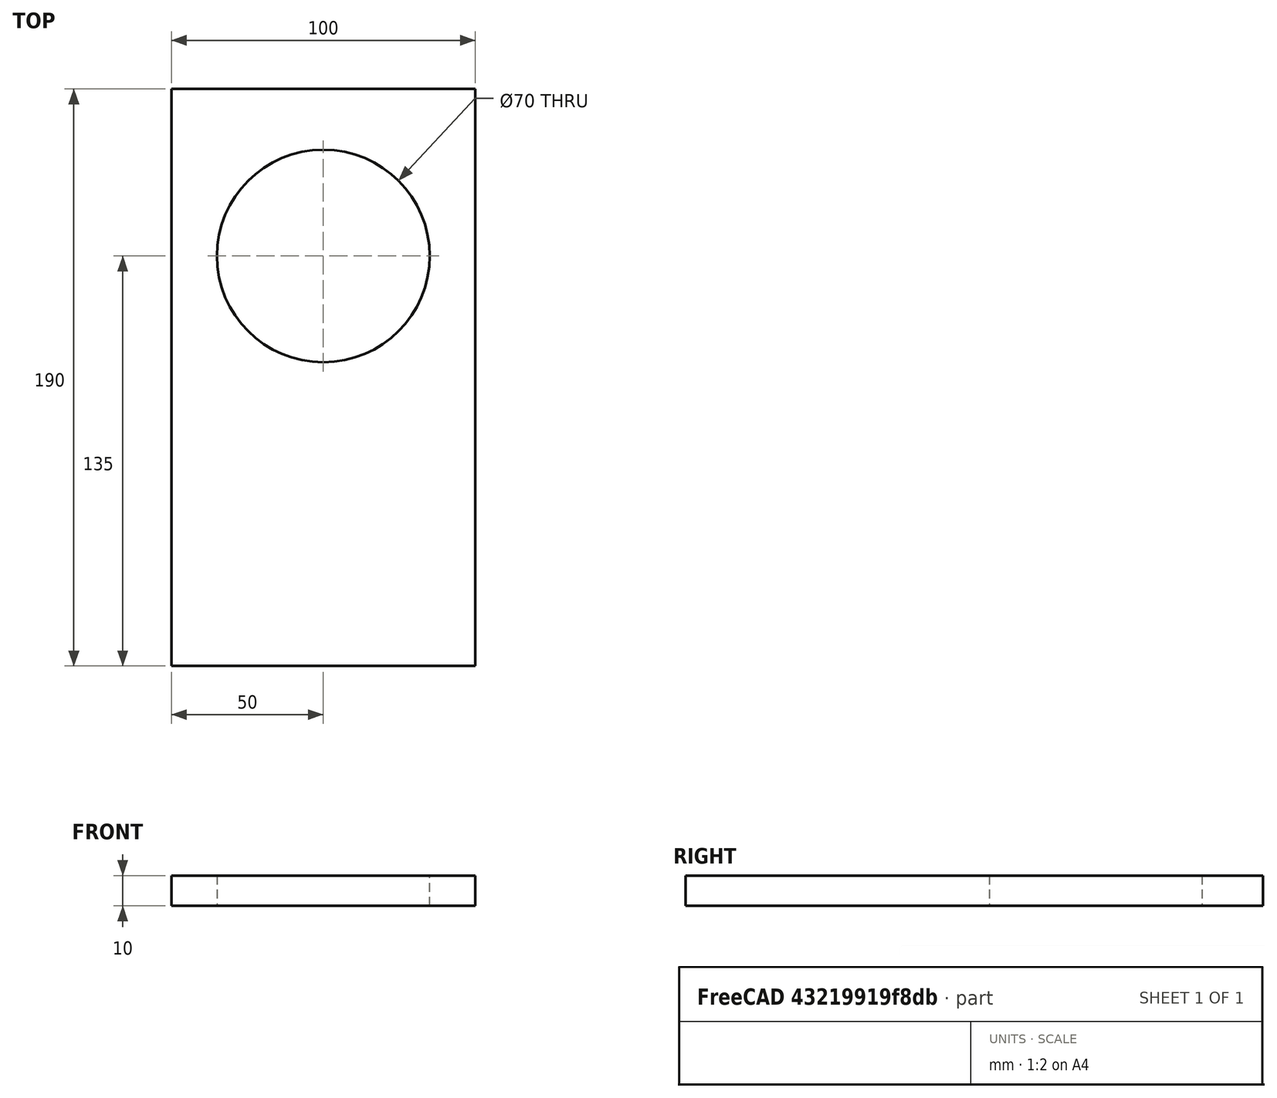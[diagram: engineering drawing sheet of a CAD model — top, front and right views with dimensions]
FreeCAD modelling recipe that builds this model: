
FCSTD DOCUMENT  (FreeCAD 0.16R6703 (Git))
Label: box_front
License: All rights reserved
LicenseURL: http://en.wikipedia.org/wiki/All_rights_reserved
objects: Sketcher::SketchObject×1, PartDesign::Pad×1
note: 3 computed .brp shape members not serialized (recipe doc carries the construction recipe); baked Part::Feature solids carry a one-line shape summary decoded from their .brp

FEATURE [Sketcher::SketchObject] Sketch
  sketch-geometry (6):
    g0: LineSegment StartX=0 StartY=0 StartZ=0 EndX=100 EndY=0 EndZ=0
    g1: LineSegment StartX=100 StartY=0 StartZ=0 EndX=100 EndY=190 EndZ=0
    g2: LineSegment StartX=100 StartY=190 StartZ=0 EndX=0 EndY=190 EndZ=0
    g3: LineSegment StartX=0 StartY=190 StartZ=0 EndX=0 EndY=0 EndZ=0
    g4: Circle CenterX=50 CenterY=135 CenterZ=0 NormalX=0 NormalY=0 NormalZ=1 Radius=35
    g5: LineSegment [constr] StartX=0 StartY=135 StartZ=0 EndX=100 EndY=135 EndZ=0
  constraints (17):
    c: Coincident(g0,g1)
    c: Coincident(g1,g2)
    c: Coincident(g2,g3)
    c: Coincident(g3,g0)
    c: Horizontal(g0)
    c: Horizontal(g2)
    c: Vertical(g1)
    c: Vertical(g3)
    c: Coincident(g0,g-1)
    c: Distance(g2) = 100
    c: Distance(g1) = 190
    c: PointOnObject(g5,g3)
    c: PointOnObject(g5,g1)
    c: Perpendicular(g3,g5)
    c: Symmetric(g5,g5,g4)
    c: Radius(g4) = 35
    c: DistanceY(g5,g2) = 55
FEATURE [PartDesign::Pad] Pad
  Length = 10
  Length2 = 100
  Sketch = -> Sketch
  Type = 0
